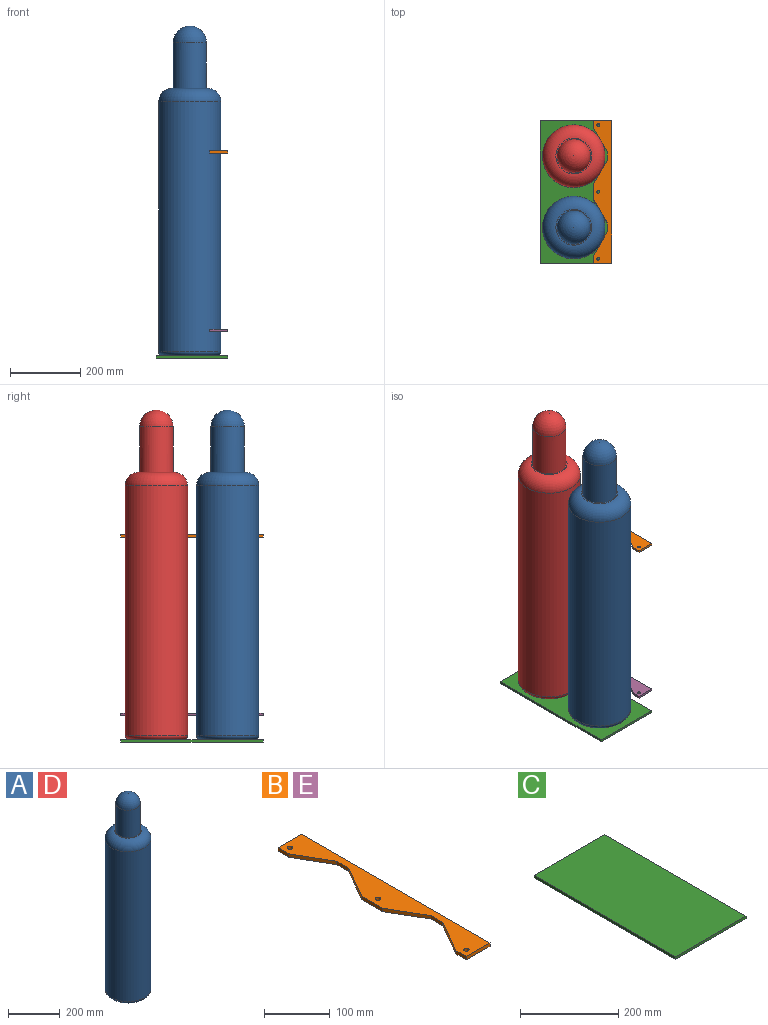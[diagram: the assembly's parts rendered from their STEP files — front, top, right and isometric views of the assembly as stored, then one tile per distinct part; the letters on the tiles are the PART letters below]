
ASSEMBLY  parts=5 mates=3
PART A: 7 faces, bbox 192.4x192.4x939.8 mm
  f0: cylinder r=88.9mm len=711.2mm, axis (0,0,-1), area 397258.7mm2, adj f5,f6
  f1: plane 101.6x101.6mm, normal (0,0,1), area 981.7mm2, adj f3,f5
  f2: plane 152.4x152.4mm, normal (0,0,-1), area 18241.5mm2, adj f6
  f3: cylinder r=47.62mm len=130.18mm, axis (0,0,-1), area 38953.1mm2, adj f1,f4
  f4: sphere r=47.62mm, area 14251.1mm2, adj f3
  f5: torus R=50.8mm, axis (0,0,1), area 28223.2mm2, adj f0,f1
  f6: torus R=76.2mm, axis (0,0,1), area 10564.6mm2, adj f0,f2
PART B: 17 faces, bbox 50.8x406.4x6.4 mm
  f0: plane 65.99x38.1mm, normal (-0.87,-0.5,0), area 483.9mm2, adj f1,f11,f12,f13
  f1: plane 25.64x6.35mm, normal (-1,0,0), area 162.8mm2, adj f0,f2,f12,f13
  f2: plane 65.99x38.1mm, normal (-0.87,0.5,0), area 483.9mm2, adj f1,f3,f12,f13
  f3: plane 45.57x6.35mm, normal (-1,0,0), area 289.4mm2, adj f2,f4,f12,f13
  f4: plane 65.99x38.1mm, normal (-0.87,-0.5,0), area 483.9mm2, adj f3,f5,f12,f13
  f5: plane 25.64x6.35mm, normal (-1,0,0), area 162.8mm2, adj f4,f6,f12,f13
  f6: plane 65.99x38.1mm, normal (-0.87,0.5,0), area 483.9mm2, adj f5,f7,f12,f13
  f7: plane 22.79x6.35mm, normal (-1,0,0), area 144.7mm2, adj f6,f8,f12,f13
  f8: plane 50.8x6.35mm, normal (0,-1,0), area 322.6mm2, adj f7,f9,f12,f13
  f9: plane 406.4x6.35mm, normal (1,0,0), area 2580.6mm2, adj f8,f10,f12,f13
  f10: plane 50.8x6.35mm, normal (0,1,0), area 322.6mm2, adj f9,f11,f12,f13
  f11: plane 22.79x6.35mm, normal (-1,0,0), area 144.7mm2, adj f0,f10,f12,f13
  f12: plane 406.4x50.8mm, normal (0,0,1), area 13514mm2, adj f0,f1,f2,f3,f4,f5,f6,f7
  f13: plane 406.4x50.8mm, normal (0,0,-1), area 13514mm2, adj f0,f1,f2,f3,f4,f5,f6,f7
  f14: cylinder r=3.97mm len=7.94mm, axis (0,0,1), area 158.3mm2, adj f12,f13
  f15: cylinder r=3.97mm len=7.94mm, axis (0,0,1), area 158.3mm2, adj f12,f13
  f16: cylinder r=3.97mm len=7.94mm, axis (0,0,1), area 158.3mm2, adj f12,f13
PART C: 6 faces, bbox 203.2x406.4x6.4 mm
  f0: plane 406.4x6.35mm, normal (1,0,0), area 2580.6mm2, adj f1,f3,f4,f5
  f1: plane 203.2x6.35mm, normal (0,1,0), area 1290.3mm2, adj f0,f2,f4,f5
  f2: plane 406.4x6.35mm, normal (-1,0,0), area 2580.6mm2, adj f1,f3,f4,f5
  f3: plane 203.2x6.35mm, normal (0,-1,0), area 1290.3mm2, adj f0,f2,f4,f5
  f4: plane 406.4x203.2mm, normal (0,0,1), area 82580.5mm2, adj f0,f1,f2,f3
  f5: plane 406.4x203.2mm, normal (0,0,-1), area 82580.5mm2, adj f0,f1,f2,f3
PART D: same geometry as A
PART E: same geometry as B
PLACE A t=(0,-101.6,-12.7)mm
PLACE B t=(0,0,565.15)mm
PLACE C t=(6.35,0,-19.05)mm
PLACE D t=(0,101.6,-12.7)mm
PLACE E t=(0,0,57.15)mm
MATE planar E.f9 <-> C.f0  axis (1,0,0) through (107.95,0,60.32)mm
MATE planar C.f4 <-> A.f0  axis (0,0,1) through (6.35,0,-12.7)mm
MATE planar B.f9 <-> E.f9  axis (1,0,0) through (107.95,0,568.32)mm
